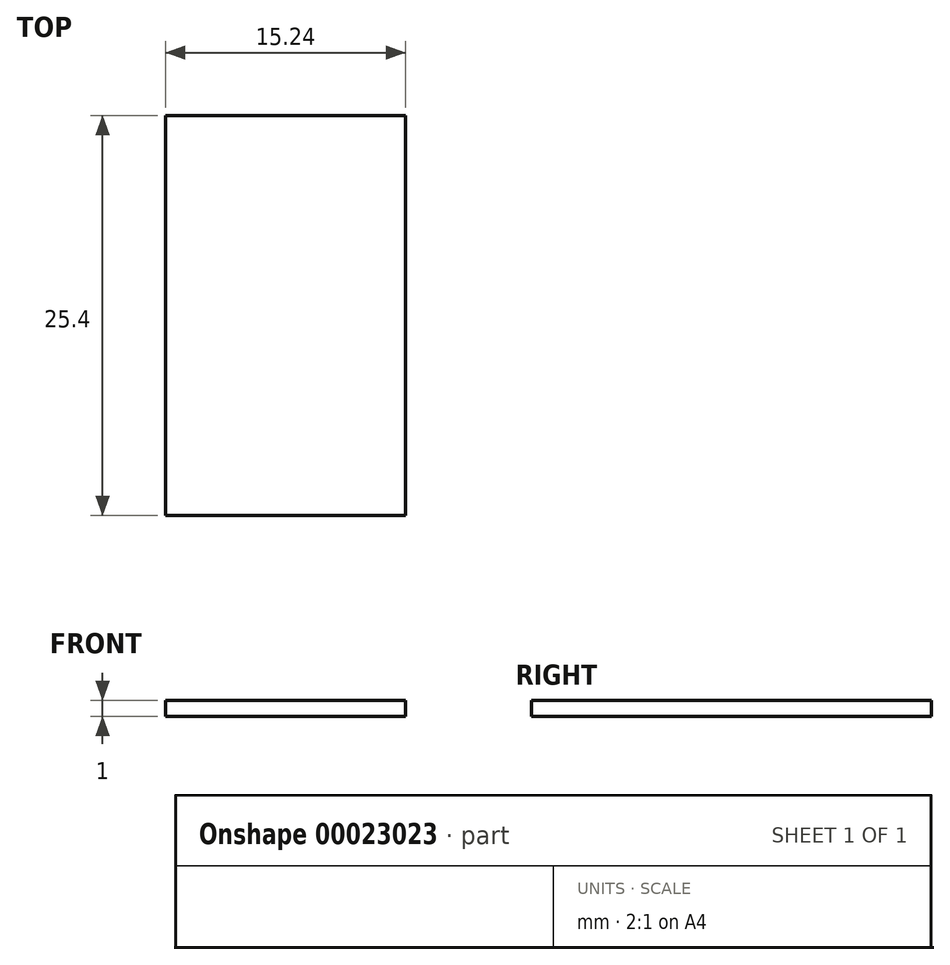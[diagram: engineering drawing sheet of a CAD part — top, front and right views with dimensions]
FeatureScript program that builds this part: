
annotation { "Feature Type Name" : "Feature", "Feature Type Description" : "" }
export const myFeature = defineFeature(function(context is Context, id is Id, definition is map)
    precondition{}
    {
        {
            var Q0;
            Q0=qCreatedBy(makeId("Top.planeOp"),FACE);
            var sketch = newSketch(context, id + "F0", { "sketchPlane" : qUnion([Q0])});
            skLineSegment(sketch, "E0.bottom", {"start": v(-7.62, 12.7) * mm, "end": v(7.62, 12.7) * mm});
            skLineSegment(sketch, "E0.top", {"start": v(-7.62, -12.7) * mm, "end": v(7.62, -12.7) * mm});
            skLineSegment(sketch, "E0.left", {"start": v(-7.62, 12.7) * mm, "end": v(-7.62, -12.7) * mm});
            skLineSegment(sketch, "E0.right", {"start": v(7.62, 12.7) * mm, "end": v(7.62, -12.7) * mm});
            skSolve(sketch);
        }
        {
            var Q0;
            Q0=makeQuery(id+"F0.imprint","IMPRINT",FACE,{"disambiguationData":[TD([[makeQuery(id+"F0.imprint","IMPRINT",EDGE,{"derivedFrom":sQuery(id+"F0.wireOp",EDGE,"E0.bottom")}),-1.0]])]});
            extrude(context, id + "F1", {"entities" : qUnion([Q0]), "depth" : 1 * mm});
        }
    });
